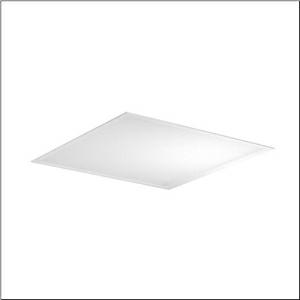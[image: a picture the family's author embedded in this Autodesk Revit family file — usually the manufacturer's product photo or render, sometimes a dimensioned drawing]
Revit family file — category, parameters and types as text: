
# Revit family: apollon_31_square_51mp12w72m42
name_source: partatom
category: Lighting Fixtures
units: mm (PartAtom-declared; Revit-internal decimal feet)

## family parameters
Cut with Voids When Loaded = No
Host = Face
Light Source = No
Part Type = Normal
Room Calculation Point = No
Round Connector Dimension = Use Diameter
Shared = No

## types (1)
- --- (1 x LED, 4000 lm, 27.5 W, 4000K)
    Apparent Load = 28 VA
    CIE Flux Codes = 62 87 97 100 100
    Color Rendering = 80
    Color Temperature = 4000K
    Default Elevation = 1800 mm
    Description = Apollon 31 square, office luminaire, primary optical cover: micro prismatic cover, of PMMA, CAT 2 (L<= 3000cd/m²), light emission: direct distribution, primary light characteristic: symmetric, installation type: lay-in mounting, recessed, LED, rated luminous flux: 4.000lm, luminous efficacy: 145lm/W, light colour: 830/840, colour temperature: 3000/4000K, control gear: ON/OFF, with terminal, 3-pole, mains connection: 220..240V, AC, 50/60Hz, rated input power: 28W, suitable for self-contained emergency lighting element 58DB00B013A with integrated self-test function according to EN 60598-2-22, housing, of aluminium, coated, traffic white (RAL 9016), module: M600, length: 595mm, width: 595mm, height: 62mm, housing upper side, of sheet steel, coated, protection rating (complete): IP20, protection rating (lamp compartment, on room side): IP40, insulation class (complete): insulation class II (safety insulation), certification: CE, ENEC, impact resistance: IK03, permissible operating ambient temperature: -20..+40°C, standard: EN 60598-2-22, corresponds to IFS (International Featured Standards) requirements for safety and quality in the food industry, packaging unit: 1 piece
    Height = 0 mm  [stored 0 ft]
    Lamp = 1 x LED
    Lamp Light Flux = 4000 lm
    Lamp Power = 27.5 W
    Lamp count = 1
    Length = 595 mm
    Luminous efficacy = 145 lm/W
    Manufacturer = Siteco
    ModVariant = No
    Model = 51MP12W72M42
    Mounting Place = Ceiling
    Mounting Type = Recessed
    Number of Poles = 1
    OnlyDefault = Yes
    Power Factor = 1
    Product Name = Apollon 31 square
    Product group = office luminaire | ceiling recessed
    ProductGroupID = 400
    Protection Class = Protection class II
    Protection Degree = IP 20
    RLX_Detail_Level = 1
    RLX_Emergency_Light_Flux = 0 lm
    RLX_Emergency_Type = 0
    RLX_Emergency_Type_DB = No
    RlxData = <blob elided: 13081 chars, md5=e3e18174>
    Socket = socket
    Standby Power = 0 W
    System Light Flux = 4000 lm
    System Power = 28 W
    Type Comments = factory setting: colour temperature 4000K
    Type Image = l_1291035.jpg
    URL = http://relux.com
    VarID = @adj_084361
    Voltage = 0 V
    Weight = 0.00 kg
    Width = 595 mm

note: [stored X ft] marks values corroborated as IEEE doubles in the binary element streams (Revit-internal decimal feet)

## geometry (parser evidence)
native form markers: Sweep x9
no freeform markers — native parametric forms only
